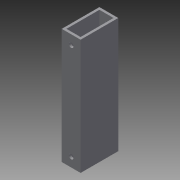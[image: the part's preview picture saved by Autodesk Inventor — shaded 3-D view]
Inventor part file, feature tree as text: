
AUTODESK INVENTOR PART (.ipt)
format: ipt  version: 2015 (Build 190159000, 159)  size: 111,616 bytes
history: native  units: in
note: dims shown in document units (in); Inventor stores cm internally (conversion verified against a paired STEP export)
features: sketch x3, extrude x2, projected_geometry x2, hole x1
ambient origin geometry x8: Origin, YZ Plane, XZ Plane, XY Plane, X Axis, Y Axis, Z Axis, Center Point
bodies: Solid1 (feature_tree)
feature tree (8):
  extrude  "Extrusion1"  Depth=2.0in
  hole  "Hole1"  [1 undecoded]
  extrude  "Extrusion2"  Depth=0.125in
  sketch  "Sketch1"  dims[d0=1.0in d1=2.0in]
  sketch  "Sketch2"  dims[d2=0.75in d3=1.75in]
  projected_geometry  "Projected Loop1"
  sketch  "Sketch3"  dims[d4=0.125in d5=0.125in d6=6.125in d7=0.0in d8=0.5in d9=0.5in d10=0.5in d11=0.5in d12=0.25in d13=0.75in d14=0.375in d15=0.25in d16=0.5635in d17=1.0in d18=0.8108in d19=3.375in d20=0.375in d21=0.375in d22=6.125in d23=0.0in]
  projected_geometry  "Projected Loop2"
note: 1 required parameter value undecoded (feature->parameter linkage not recoverable at this tier; creation-order binding heuristic only, values carry confidence <= 0.55)
